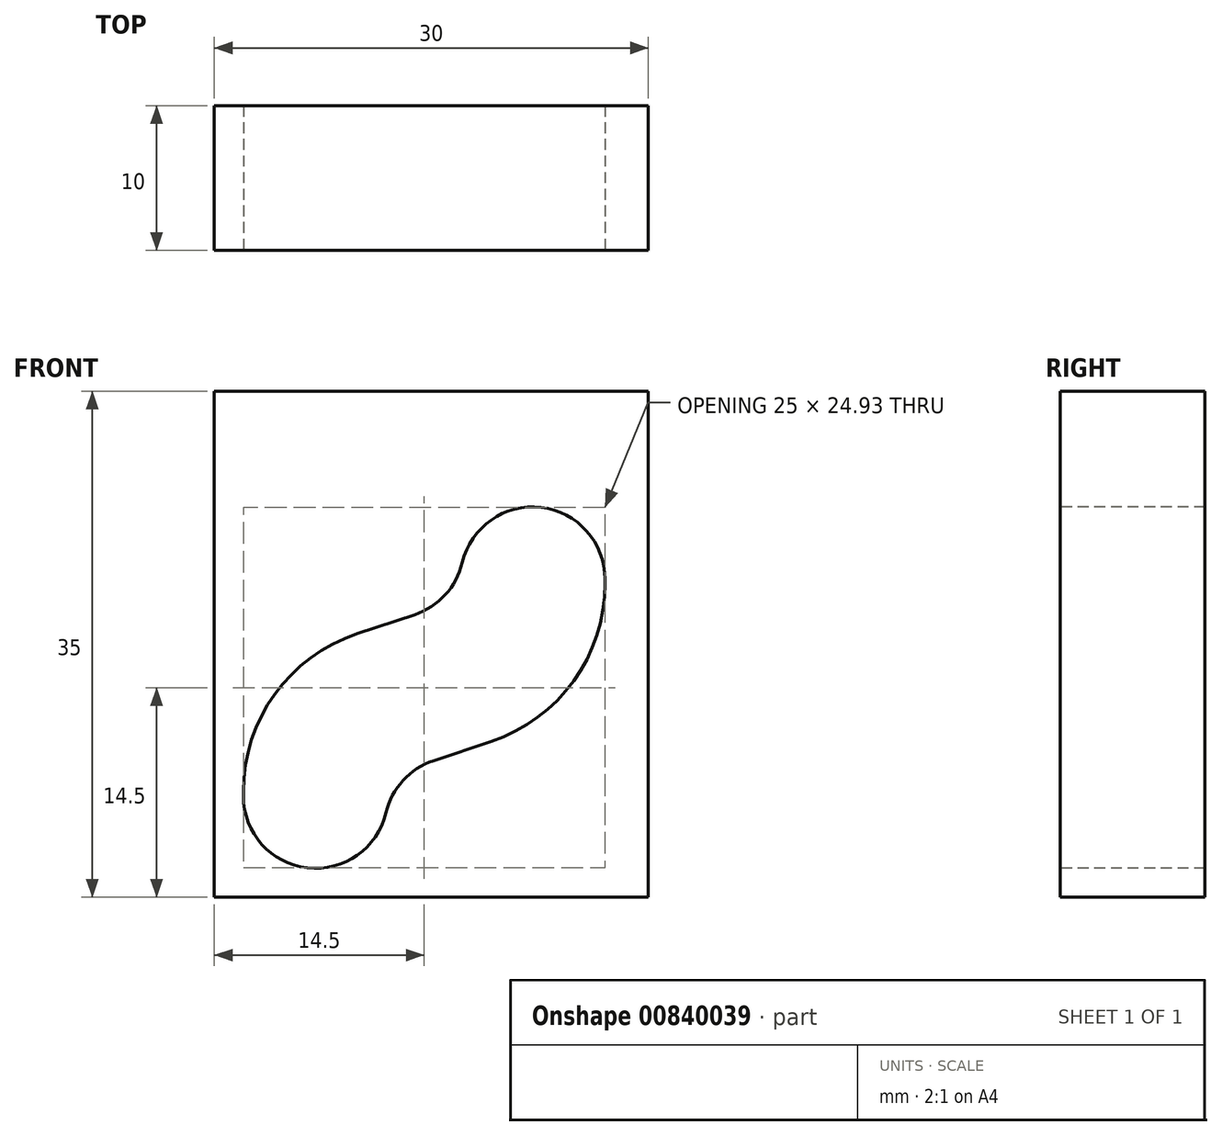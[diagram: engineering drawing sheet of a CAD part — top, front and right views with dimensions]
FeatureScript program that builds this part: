
annotation { "Feature Type Name" : "Feature", "Feature Type Description" : "" }
export const myFeature = defineFeature(function(context is Context, id is Id, definition is map)
    precondition{}
    {
        {
            var Q0;
            Q0=qCreatedBy(makeId("Front.planeOp"),FACE);
            var sketch = newSketch(context, id + "F0", { "sketchPlane" : qUnion([Q0])});
            skLineSegment(sketch, "E0.bottom", {"start": v(0, 0) * mm, "end": v(30, 0) * mm});
            skLineSegment(sketch, "E0.top", {"start": v(0, 35) * mm, "end": v(30, 35) * mm});
            skLineSegment(sketch, "E0.left", {"start": v(0, 0) * mm, "end": v(0, 35) * mm});
            skLineSegment(sketch, "E0.right", {"start": v(30, 0) * mm, "end": v(30, 35) * mm});
            skSolve(sketch);
        }
        {
            var Q0;
            Q0 = qSketchRegion(id + "F0", true);
            extrude(context, id + "F1", {"entities" : qUnion([Q0]), "depth" : 10 * mm, "offsetDistance" : 25 * mm});
        }
        {
            var Q0;
            Q0=makeQuery(id+"F1.opExtrude","CAP_FACE",FACE,{"disambiguationData":[OSD([sQuery(id+"F0.wireOp",EDGE,"E0.bottom"),sQuery(id+"F0.wireOp",EDGE,"E0.top"),sQuery(id+"F0.wireOp",EDGE,"E0.left"),sQuery(id+"F0.wireOp",EDGE,"E0.right")])],"isStart":false});
            var sketch = newSketch(context, id + "F2", { "sketchPlane" : qUnion([Q0])});
            skArc(sketch, "E1", {"start": v(2, 7) * mm, "mid": v(6.42, 2.03) * mm, "end": v(11.87, 5.85) * mm});
            skArc(sketch, "E2", {"start": v(27, 22) * mm, "mid": v(22.58, 26.97) * mm, "end": v(17.13, 23.15) * mm});
            skLineSegment(sketch, "E3", {"start": v(7, 7) * mm, "end": v(7, 12) * mm, "construction": true});
            skLineSegment(sketch, "E4", {"start": v(22, 22) * mm, "end": v(22, 17) * mm, "construction": true});
            skLineSegment(sketch, "E5", {"start": v(22, 17) * mm, "end": v(7, 12) * mm, "construction": true});
            skLineSegment(sketch, "E6.0", {"start": v(27, 22) * mm, "end": v(27, 21.68) * mm});
            skLineSegment(sketch, "E7.0", {"start": v(19.14, 10.78) * mm, "end": v(15.15, 9.45) * mm});
            skLineSegment(sketch, "E8.0", {"start": v(13.85, 19.55) * mm, "end": v(9.86, 18.22) * mm});
            skLineSegment(sketch, "E9.0", {"start": v(2, 7) * mm, "end": v(2, 7.32) * mm});
            skArc(sketch, "E10.filletArc", {"start": v(15.15, 9.45) * mm, "mid": v(13.04, 8.08) * mm, "end": v(11.87, 5.85) * mm});
            skArc(sketch, "E11.filletArc", {"start": v(13.85, 19.55) * mm, "mid": v(15.96, 20.92) * mm, "end": v(17.13, 23.15) * mm});
            skArc(sketch, "E12.filletArc", {"start": v(19.14, 10.78) * mm, "mid": v(24.83, 14.96) * mm, "end": v(27, 21.68) * mm});
            skArc(sketch, "E13.filletArc", {"start": v(9.86, 18.22) * mm, "mid": v(4.17, 14.04) * mm, "end": v(2, 7.32) * mm});
            skSolve(sketch);
        }
        {
            var Q0;
            Q0 = qSketchRegion(id + "F2", true);
            extrude(context, id + "F3", {"entities" : qUnion([Q0]), "operationType" : NewBodyOperationType.REMOVE, "endBound" : BoundingType.THROUGH_ALL, "oppositeDirection" : true, "depth" : 25 * mm, "offsetDistance" : 25 * mm});
        }
    });
